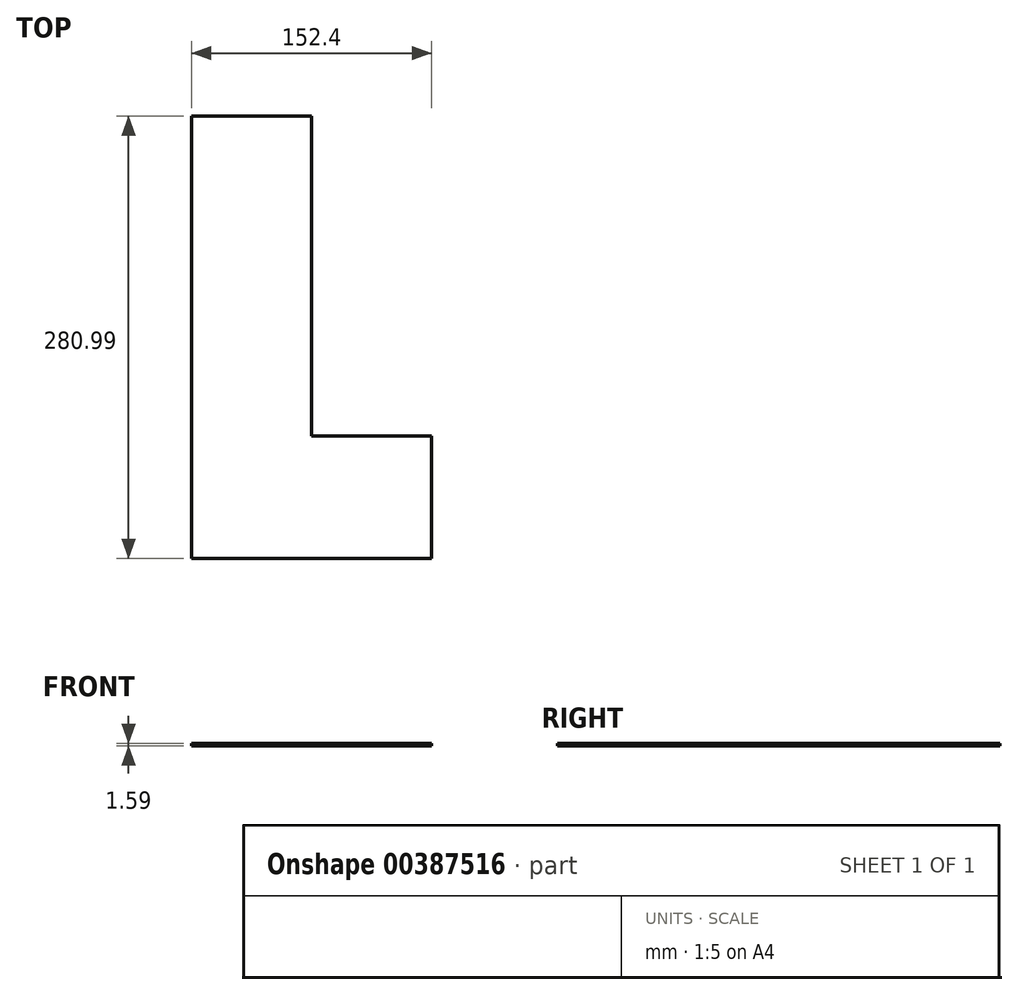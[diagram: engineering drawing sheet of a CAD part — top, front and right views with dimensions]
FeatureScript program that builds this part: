
annotation { "Feature Type Name" : "Feature", "Feature Type Description" : "" }
export const myFeature = defineFeature(function(context is Context, id is Id, definition is map)
    precondition{}
    {
        {
            var Q0;
            Q0=qCreatedBy(makeId("Top.planeOp"),FACE);
            var sketch = newSketch(context, id + "F0", { "sketchPlane" : qUnion([Q0])});
            skLineSegment(sketch, "E0.bottom", {"start": v(0, 0) * mm, "end": v(152.4, 0) * mm});
            skLineSegment(sketch, "E0.top", {"start": v(0, 280.99) * mm, "end": v(152.4, 280.99) * mm});
            skLineSegment(sketch, "E0.left", {"start": v(0, 0) * mm, "end": v(0, 280.99) * mm});
            skLineSegment(sketch, "E0.right", {"start": v(152.4, 0) * mm, "end": v(152.4, 280.99) * mm});
            skLineSegment(sketch, "E1.bottom", {"start": v(152.4, 280.99) * mm, "end": v(76.2, 280.99) * mm});
            skLineSegment(sketch, "E1.top", {"start": v(152.4, 77.79) * mm, "end": v(76.2, 77.79) * mm});
            skLineSegment(sketch, "E1.left", {"start": v(152.4, 280.99) * mm, "end": v(152.4, 77.79) * mm});
            skLineSegment(sketch, "E1.right", {"start": v(76.2, 280.99) * mm, "end": v(76.2, 77.79) * mm});
            skSolve(sketch);
        }
        {
            var Q0;
            Q0=makeQuery(id+"F0.imprint","IMPRINT",FACE,{"disambiguationData":[TD([[makeQuery(id+"F0.imprint","IMPRINT",EDGE,{"derivedFrom":sQuery(id+"F0.wireOp",EDGE,"E0.bottom")}),1.0]])]});
            extrude(context, id + "F1", {"entities" : qUnion([Q0]), "depth" : 1.59 * mm});
        }
    });
